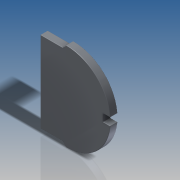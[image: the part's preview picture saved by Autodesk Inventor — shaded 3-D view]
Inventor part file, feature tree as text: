
AUTODESK INVENTOR PART (.ipt)
format: ipt  version: 2016 SP2 (Build 200236200, 236)  size: 237,056 bytes
history: native  units: in
note: dims shown in document units (in); Inventor stores cm internally (conversion verified against a paired STEP export)
features: extrude x3, sketch x2, fillet x1
ambient origin geometry x8: Origin, YZ Plane, XZ Plane, XY Plane, X Axis, Y Axis, Z Axis, Center Point
bodies: Solid1 (feature_tree)
feature tree (6):
  sketch  "Sketch2"  dims[d0=0.378in d1=0.063in]
  extrude  "Extrusion1"  Depth=0.378in
  extrude  "Extrusion2"  Depth=0.0039in
  extrude  "Extrusion3"  Depth=0.3786in
  fillet  "Fillet1"  Radius=0.6929in
  sketch  "Sketch3"  dims[d2=0.315in d3=0.5354in d4=0.3786in d5=0.6929in d6=45.0deg d7=0.0315in d8=0.2205in d9=0.0472in d10=0.063in d11=0.0in d12=0.0472in d13=0.0in d14=0.0472in d15=0.1575in d16=0.189in d17=0.0in d18=0.0039in]
